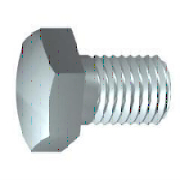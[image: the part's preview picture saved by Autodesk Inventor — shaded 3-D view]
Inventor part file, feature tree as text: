
AUTODESK INVENTOR PART (.ipt)
format: ipt  version: 2023 (Build 270158000, 158)  size: 216,064 bytes
history: native  units: mm
features: sketch x4, extrude x2, other x2, revolve x1, thread x1, chamfer x1, plane x1, split x1, surface_op x1
ambient origin geometry x8: Origin, YZ Plane, XZ Plane, XY Plane, X Axis, Y Axis, Z Axis, Center Point
bodies: Solid1 (feature_tree)
feature tree (14):
  revolve  "Revolution1"  [1 undecoded]
  thread  "Thread1"  [1 undecoded]
  chamfer  "Chamfer1"  Angle=90.0deg  [1 undecoded]
  extrude  "Extrusion1"  Depth=10.0mm
  plane  "Work Plane1"
  split  "Split1"
  sketch  "Sketch1"  dims[d6=0.6mm d7=11.63mm d8=0.1mm]
  sketch  "Sketch2"  dims[d9=135.0deg]
  sketch  "Sketch4"  dims[d11=40.0mm d13=90.0deg d14=22.0mm d15=0.0mm d16=0.6mm d17=2.0mm d18=45.0deg d19=13.0mm d20=15.011107mm d21=4.7mm d22=0.0mm d32=9.2mm d34=0.0mm d35=8.0mm d36=0.0mm d37=0.0mm d38=0.0mm d39=120.0deg d40=13.0mm d41=10.0mm d42=60.0deg d49=0.6mm]
  other  "Srf2"
  sketch  "Sketch3"  dims[d10=8.0mm]
  other  "Srf1"
  extrude  "ExtrusionSrf1"  TaperAngle=0.0deg  [1 undecoded]
  surface_op  "Boundary Patch1"
note: 4 required parameter values undecoded (feature->parameter linkage not recoverable at this tier; creation-order binding heuristic only, values carry confidence <= 0.55)